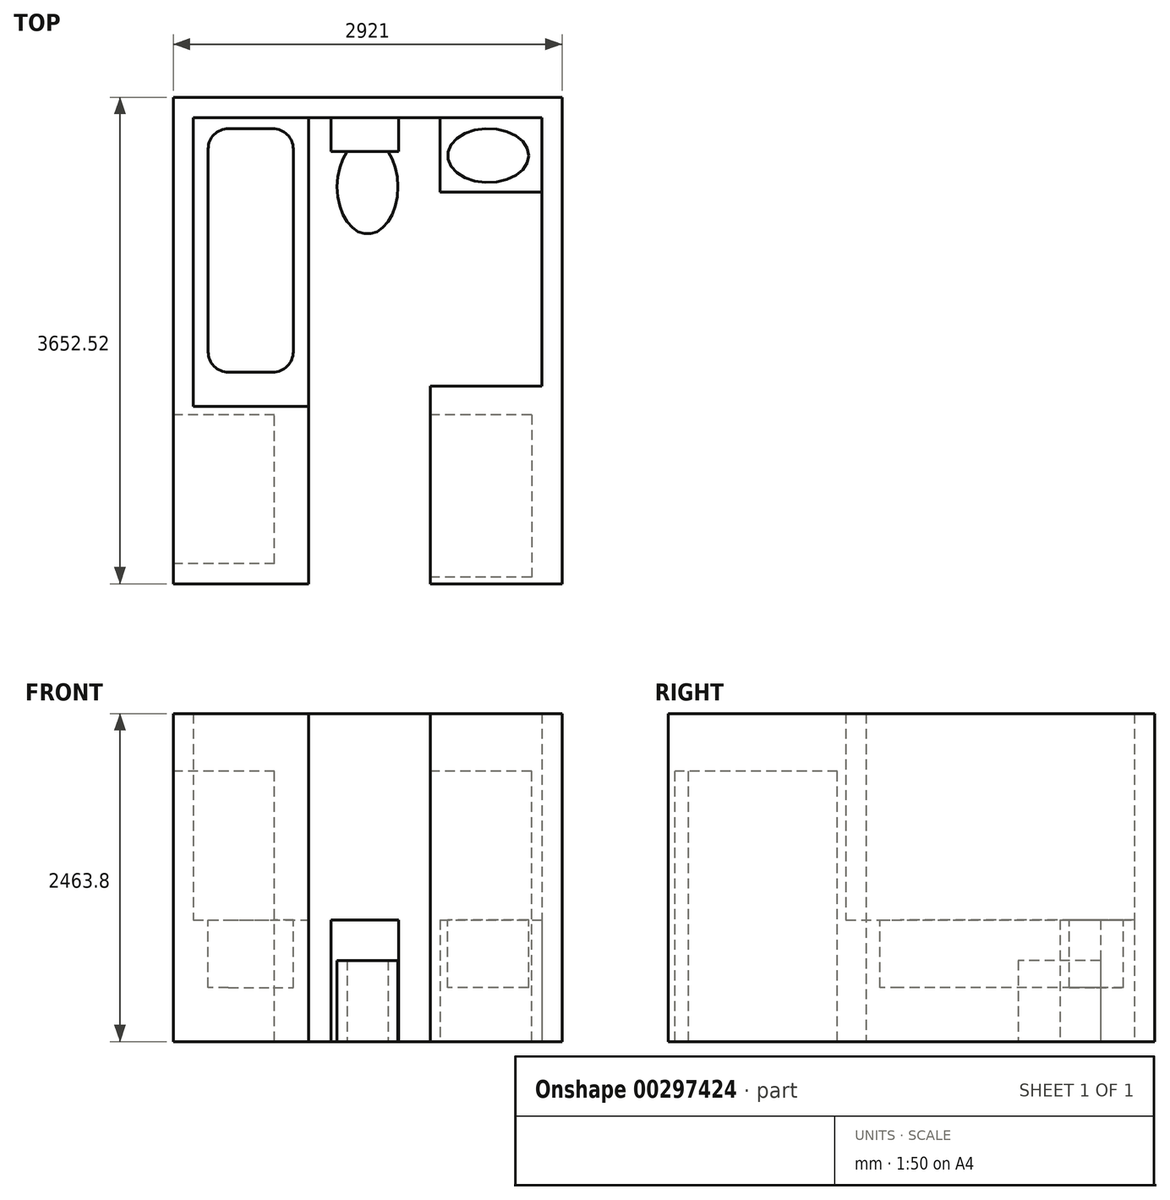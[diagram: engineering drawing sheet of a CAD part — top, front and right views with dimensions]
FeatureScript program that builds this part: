
annotation { "Feature Type Name" : "Feature", "Feature Type Description" : "" }
export const myFeature = defineFeature(function(context is Context, id is Id, definition is map)
    precondition{}
    {
        {
            var Q0;
            Q0=qCreatedBy(makeId("Top.planeOp"),FACE);
            var sketch = newSketch(context, id + "F0", { "sketchPlane" : qUnion([Q0])});
            skLineSegment(sketch, "E0.bottom", {"start": v(-1198.42, 0) * mm, "end": v(-334.82, 0) * mm});
            skLineSegment(sketch, "E0.top", {"start": v(-1350.82, -1333.5) * mm, "end": v(-334.82, -1333.5) * mm});
            skLineSegment(sketch, "E0.left", {"start": v(-1350.82, 0) * mm, "end": v(-1350.82, -1333.5) * mm});
            skLineSegment(sketch, "E0.right", {"start": v(-334.82, 0) * mm, "end": v(-334.82, -1333.5) * mm});
            skLineSegment(sketch, "E1.bottom", {"start": v(579.58, 0) * mm, "end": v(1417.78, 0) * mm});
            skLineSegment(sketch, "E1.top", {"start": v(579.58, -1333.5) * mm, "end": v(1570.18, -1333.5) * mm});
            skLineSegment(sketch, "E1.left", {"start": v(579.58, 0) * mm, "end": v(579.58, -1333.5) * mm});
            skLineSegment(sketch, "E1.right", {"start": v(1570.18, 0) * mm, "end": v(1570.18, -1333.5) * mm});
            skLineSegment(sketch, "E2", {"start": v(-1350.82, 0) * mm, "end": v(-1350.82, 2319.02) * mm});
            skLineSegment(sketch, "E3", {"start": v(-1350.82, 2319.02) * mm, "end": v(1570.18, 2319.02) * mm});
            skLineSegment(sketch, "E4", {"start": v(1570.18, 0) * mm, "end": v(1570.18, 2319.02) * mm});
            skLineSegment(sketch, "E5.0", {"start": v(-1198.42, 0) * mm, "end": v(-1198.42, 2166.62) * mm});
            skLineSegment(sketch, "E6.0", {"start": v(-1198.42, 2166.62) * mm, "end": v(1417.78, 2166.62) * mm});
            skLineSegment(sketch, "E7.0", {"start": v(1417.78, 0) * mm, "end": v(1417.78, 2166.62) * mm});
            skSolve(sketch);
        }
        {
            var Q0;
            Q0=qSketchRegion(id+"F0",true);
            extrude(context, id + "F1", {"entities" : qUnion([Q0]), "depth" : 2463.8 * mm});
        }
        {
            var Q0;
            Q0=makeQuery(id+"F1.opExtrude","SWEPT_FACE",FACE,{"disambiguationData":[OSD([sQuery(id+"F0.wireOp",EDGE,"E0.left"),sQuery(id+"F0.wireOp",EDGE,"E2")])]});
            var sketch = newSketch(context, id + "F2", { "sketchPlane" : qUnion([Q0])});
            skLineSegment(sketch, "E8.bottom", {"start": v(63.5, 0) * mm, "end": v(1181.1, 0) * mm});
            skLineSegment(sketch, "E8.top", {"start": v(63.5, 2032) * mm, "end": v(1181.1, 2032) * mm});
            skLineSegment(sketch, "E8.left", {"start": v(63.5, 0) * mm, "end": v(63.5, 2032) * mm});
            skLineSegment(sketch, "E8.right", {"start": v(1181.1, 0) * mm, "end": v(1181.1, 2032) * mm});
            skSolve(sketch);
        }
        {
            var Q0;
            Q0=makeQuery(id+"F2.imprint","IMPRINT",FACE,{"disambiguationData":[TD([[makeQuery(id+"F2.imprint","IMPRINT",EDGE,{"derivedFrom":sQuery(id+"F2.wireOp",EDGE,"E8.bottom")}),-1.0]])]});
            extrude(context, id + "F3", {"entities" : qUnion([Q0]), "operationType" : NewBodyOperationType.REMOVE, "oppositeDirection" : true, "depth" : 762 * mm});
        }
        {
            var Q0;
            Q0=makeQuery(id+"F1.opExtrude","SWEPT_FACE",FACE,{"disambiguationData":[OSD([sQuery(id+"F0.wireOp",EDGE,"E1.left")])]});
            var sketch = newSketch(context, id + "F4", { "sketchPlane" : qUnion([Q0])});
            skLineSegment(sketch, "E9.bottom", {"start": v(63.5, 0) * mm, "end": v(1282.7, 0) * mm});
            skLineSegment(sketch, "E9.top", {"start": v(63.5, 2032) * mm, "end": v(1282.7, 2032) * mm});
            skLineSegment(sketch, "E9.left", {"start": v(63.5, 0) * mm, "end": v(63.5, 2032) * mm});
            skLineSegment(sketch, "E9.right", {"start": v(1282.7, 0) * mm, "end": v(1282.7, 2032) * mm});
            skSolve(sketch);
        }
        {
            var Q0;
            Q0=makeQuery(id+"F4.imprint","IMPRINT",FACE,{"disambiguationData":[TD([[makeQuery(id+"F4.imprint","IMPRINT",EDGE,{"derivedFrom":sQuery(id+"F4.wireOp",EDGE,"E9.bottom")}),1.0]])]});
            extrude(context, id + "F5", {"entities" : qUnion([Q0]), "operationType" : NewBodyOperationType.REMOVE, "oppositeDirection" : true, "depth" : 762 * mm});
        }
        {
            var Q0;
            Q0=makeQuery(id+"F1.opExtrude","CAP_FACE",FACE,{"disambiguationData":[OSD([sQuery(id+"F0.wireOp",EDGE,"E0.bottom"),sQuery(id+"F0.wireOp",EDGE,"E0.top"),sQuery(id+"F0.wireOp",EDGE,"E0.left"),sQuery(id+"F0.wireOp",EDGE,"E0.right"),sQuery(id+"F0.wireOp",EDGE,"E1.bottom"),sQuery(id+"F0.wireOp",EDGE,"E1.top"),sQuery(id+"F0.wireOp",EDGE,"E1.left"),sQuery(id+"F0.wireOp",EDGE,"E1.right"),sQuery(id+"F0.wireOp",EDGE,"E2"),sQuery(id+"F0.wireOp",EDGE,"E3"),sQuery(id+"F0.wireOp",EDGE,"E4"),sQuery(id+"F0.wireOp",EDGE,"E5.0"),sQuery(id+"F0.wireOp",EDGE,"E6.0"),sQuery(id+"F0.wireOp",EDGE,"E7.0")])],"isStart":true});
            var sketch = newSketch(context, id + "F6", { "sketchPlane" : qUnion([Q0])});
            skLineSegment(sketch, "E10.bottom", {"start": v(1417.78, -2166.62) * mm, "end": v(655.78, -2166.62) * mm});
            skLineSegment(sketch, "E10.top", {"start": v(1417.78, -1607.82) * mm, "end": v(655.78, -1607.82) * mm});
            skLineSegment(sketch, "E10.left", {"start": v(1417.78, -2166.62) * mm, "end": v(1417.78, -1607.82) * mm});
            skLineSegment(sketch, "E10.right", {"start": v(655.78, -2166.62) * mm, "end": v(655.78, -1607.82) * mm});
            skLineSegment(sketch, "E11.bottom", {"start": v(-1198.42, -2166.62) * mm, "end": v(-334.82, -2166.62) * mm});
            skLineSegment(sketch, "E11.top", {"start": v(-1198.42, 0) * mm, "end": v(-334.82, 0) * mm});
            skLineSegment(sketch, "E11.left", {"start": v(-1198.42, -2166.62) * mm, "end": v(-1198.42, 0) * mm});
            skLineSegment(sketch, "E11.right", {"start": v(-334.82, -2166.62) * mm, "end": v(-334.82, 0) * mm});
            skLineSegment(sketch, "E12.bottom", {"start": v(-165.39, -2166.62) * mm, "end": v(342.61, -2166.62) * mm});
            skLineSegment(sketch, "E12.top", {"start": v(-165.39, -1912.62) * mm, "end": v(342.61, -1912.62) * mm});
            skLineSegment(sketch, "E12.left", {"start": v(-165.39, -2166.62) * mm, "end": v(-165.39, -1912.62) * mm});
            skLineSegment(sketch, "E12.right", {"start": v(342.61, -2166.62) * mm, "end": v(342.61, -1912.62) * mm});
            skSolve(sketch);
        }
        {
            var Q0;
            Q0=qSketchRegion(id+"F6",true);
            extrude(context, id + "F7", {"entities" : qUnion([Q0]), "operationType" : NewBodyOperationType.ADD, "oppositeDirection" : true, "depth" : 914.4 * mm});
        }
        {
            var Q0;
            Q0=makeQuery(id+"F7.boolean.opBoolean","MERGE",FACE,{"derivedFrom":[makeQuery(id+"F1.opExtrude","CAP_FACE",FACE,{"disambiguationData":[OSD([sQuery(id+"F0.wireOp",EDGE,"E0.bottom"),sQuery(id+"F0.wireOp",EDGE,"E0.top"),sQuery(id+"F0.wireOp",EDGE,"E0.left"),sQuery(id+"F0.wireOp",EDGE,"E0.right"),sQuery(id+"F0.wireOp",EDGE,"E1.bottom"),sQuery(id+"F0.wireOp",EDGE,"E1.top"),sQuery(id+"F0.wireOp",EDGE,"E1.left"),sQuery(id+"F0.wireOp",EDGE,"E1.right"),sQuery(id+"F0.wireOp",EDGE,"E2"),sQuery(id+"F0.wireOp",EDGE,"E3"),sQuery(id+"F0.wireOp",EDGE,"E4"),sQuery(id+"F0.wireOp",EDGE,"E5.0"),sQuery(id+"F0.wireOp",EDGE,"E6.0"),sQuery(id+"F0.wireOp",EDGE,"E7.0")])],"isStart":true}),makeQuery(id+"F7.opExtrude","CAP_FACE",FACE,{"disambiguationData":[OSD([sQuery(id+"F6.wireOp",EDGE,"E10.bottom"),sQuery(id+"F6.wireOp",EDGE,"E10.top"),sQuery(id+"F6.wireOp",EDGE,"E10.left"),sQuery(id+"F6.wireOp",EDGE,"E10.right")])],"isStart":true}),makeQuery(id+"F7.opExtrude","CAP_FACE",FACE,{"disambiguationData":[OSD([sQuery(id+"F6.wireOp",EDGE,"E11.bottom"),sQuery(id+"F6.wireOp",EDGE,"E11.top"),sQuery(id+"F6.wireOp",EDGE,"E11.left"),sQuery(id+"F6.wireOp",EDGE,"E11.right")])],"isStart":true}),makeQuery(id+"F7.opExtrude","CAP_FACE",FACE,{"disambiguationData":[OSD([sQuery(id+"F6.wireOp",EDGE,"E12.bottom"),sQuery(id+"F6.wireOp",EDGE,"E12.top"),sQuery(id+"F6.wireOp",EDGE,"E12.left"),sQuery(id+"F6.wireOp",EDGE,"E12.right")])],"isStart":true})]});
            var sketch = newSketch(context, id + "F8", { "sketchPlane" : qUnion([Q0])});
            skEllipse(sketch, "E13", {"center": v(109.68, -1649.28) * mm, "majorRadius": 355.6 * mm, "minorRadius": 228.6 * mm, "majorAxis": v(0, 1)});
            skSolve(sketch);
        }
        {
            var Q0;
            Q0=qSketchRegion(id+"F8",true);
            extrude(context, id + "F9", {"entities" : qUnion([Q0]), "operationType" : NewBodyOperationType.ADD, "oppositeDirection" : true, "depth" : 609.6 * mm});
        }
        {
            var Q0;
            Q0=makeQuery(id+"F7.opExtrude","CAP_FACE",FACE,{"disambiguationData":[OSD([sQuery(id+"F6.wireOp",EDGE,"E11.bottom"),sQuery(id+"F6.wireOp",EDGE,"E11.top"),sQuery(id+"F6.wireOp",EDGE,"E11.left"),sQuery(id+"F6.wireOp",EDGE,"E11.right")])],"isStart":false});
            var sketch = newSketch(context, id + "F10", { "sketchPlane" : qUnion([Q0])});
            skLineSegment(sketch, "E14.bottom", {"start": v(-935.5, 2085.16) * mm, "end": v(-601.52, 2085.16) * mm});
            skLineSegment(sketch, "E14.top", {"start": v(-935.5, 256.36) * mm, "end": v(-601.52, 256.36) * mm});
            skLineSegment(sketch, "E14.left", {"start": v(-1087.9, 1932.76) * mm, "end": v(-1087.9, 408.76) * mm});
            skLineSegment(sketch, "E15", {"start": v(-449.12, 1932.76) * mm, "end": v(-449.12, 408.76) * mm});
            skPoint(sketch, "E16.visualSharp", {"position": v(-1087.9, 2085.16) * mm});
            skArc(sketch, "E16.filletArc", {"start": v(-935.5, 2085.16) * mm, "mid": v(-1043.26, 2040.52) * mm, "end": v(-1087.9, 1932.76) * mm});
            skPoint(sketch, "E17.visualSharp", {"position": v(-449.12, 2085.16) * mm});
            skArc(sketch, "E17.filletArc", {"start": v(-449.12, 1932.76) * mm, "mid": v(-493.76, 2040.52) * mm, "end": v(-601.52, 2085.16) * mm});
            skPoint(sketch, "E18.visualSharp", {"position": v(-1087.9, 256.36) * mm});
            skArc(sketch, "E18.filletArc", {"start": v(-1087.9, 408.76) * mm, "mid": v(-1043.26, 301) * mm, "end": v(-935.5, 256.36) * mm});
            skPoint(sketch, "E19.visualSharp", {"position": v(-449.12, 256.36) * mm});
            skArc(sketch, "E19.filletArc", {"start": v(-601.52, 256.36) * mm, "mid": v(-493.76, 301) * mm, "end": v(-449.12, 408.76) * mm});
            skEllipse(sketch, "E20", {"center": v(1016.17, 1882.7) * mm, "majorRadius": 304.8 * mm, "minorRadius": 203.2 * mm, "majorAxis": v(1, 0)});
            skSolve(sketch);
        }
        {
            var Q0;
            Q0=qSketchRegion(id+"F10",true);
            extrude(context, id + "F11", {"entities" : qUnion([Q0]), "operationType" : NewBodyOperationType.REMOVE, "oppositeDirection" : true, "depth" : 508 * mm});
        }
        {
            var Q0;
            Q0=makeQuery(id+"F9.boolean.opBoolean","MERGE",FACE,{"derivedFrom":[makeQuery(id+"F7.boolean.opBoolean","MERGE",FACE,{"derivedFrom":[makeQuery(id+"F1.opExtrude","CAP_FACE",FACE,{"disambiguationData":[OSD([sQuery(id+"F0.wireOp",EDGE,"E0.bottom"),sQuery(id+"F0.wireOp",EDGE,"E0.top"),sQuery(id+"F0.wireOp",EDGE,"E0.left"),sQuery(id+"F0.wireOp",EDGE,"E0.right"),sQuery(id+"F0.wireOp",EDGE,"E1.bottom"),sQuery(id+"F0.wireOp",EDGE,"E1.top"),sQuery(id+"F0.wireOp",EDGE,"E1.left"),sQuery(id+"F0.wireOp",EDGE,"E1.right"),sQuery(id+"F0.wireOp",EDGE,"E2"),sQuery(id+"F0.wireOp",EDGE,"E3"),sQuery(id+"F0.wireOp",EDGE,"E4"),sQuery(id+"F0.wireOp",EDGE,"E5.0"),sQuery(id+"F0.wireOp",EDGE,"E6.0"),sQuery(id+"F0.wireOp",EDGE,"E7.0")])],"isStart":true}),makeQuery(id+"F7.opExtrude","CAP_FACE",FACE,{"disambiguationData":[OSD([sQuery(id+"F6.wireOp",EDGE,"E10.bottom"),sQuery(id+"F6.wireOp",EDGE,"E10.top"),sQuery(id+"F6.wireOp",EDGE,"E10.left"),sQuery(id+"F6.wireOp",EDGE,"E10.right")])],"isStart":true}),makeQuery(id+"F7.opExtrude","CAP_FACE",FACE,{"disambiguationData":[OSD([sQuery(id+"F6.wireOp",EDGE,"E11.bottom"),sQuery(id+"F6.wireOp",EDGE,"E11.top"),sQuery(id+"F6.wireOp",EDGE,"E11.left"),sQuery(id+"F6.wireOp",EDGE,"E11.right")])],"isStart":true}),makeQuery(id+"F7.opExtrude","CAP_FACE",FACE,{"disambiguationData":[OSD([sQuery(id+"F6.wireOp",EDGE,"E12.bottom"),sQuery(id+"F6.wireOp",EDGE,"E12.top"),sQuery(id+"F6.wireOp",EDGE,"E12.left"),sQuery(id+"F6.wireOp",EDGE,"E12.right")])],"isStart":true})]}),makeQuery(id+"F9.opExtrude","CAP_FACE",FACE,{"disambiguationData":[OSD([sQuery(id+"F8.wireOp",EDGE,"E13")])],"isStart":true})]});
            var sketch = newSketch(context, id + "F12", { "sketchPlane" : qUnion([Q0])});
            skLineSegment(sketch, "E21.bottom", {"start": v(579.58, 0) * mm, "end": v(1417.78, 0) * mm});
            skLineSegment(sketch, "E21.top", {"start": v(579.58, -152.4) * mm, "end": v(1417.78, -152.4) * mm});
            skLineSegment(sketch, "E21.left", {"start": v(579.58, 0) * mm, "end": v(579.58, -152.4) * mm});
            skLineSegment(sketch, "E21.right", {"start": v(1417.78, 0) * mm, "end": v(1417.78, -152.4) * mm});
            skLineSegment(sketch, "E22.bottom", {"start": v(-1198.42, 0) * mm, "end": v(-1350.82, 0) * mm});
            skLineSegment(sketch, "E22.top", {"start": v(-1198.42, -152.4) * mm, "end": v(-1350.82, -152.4) * mm});
            skLineSegment(sketch, "E22.left", {"start": v(-1350.82, 0) * mm, "end": v(-1350.82, -152.4) * mm});
            skLineSegment(sketch, "E22.right", {"start": v(-1198.42, 0) * mm, "end": v(-1198.42, -152.4) * mm});
            skSolve(sketch);
        }
        {
            var Q0;
            Q0=qSketchRegion(id+"F12",true);
            var Q1;
            Q1=makeQuery(id+"F1.opExtrude","CAP_FACE",FACE,{"disambiguationData":[OSD([sQuery(id+"F0.wireOp",EDGE,"E0.bottom"),sQuery(id+"F0.wireOp",EDGE,"E0.top"),sQuery(id+"F0.wireOp",EDGE,"E0.left"),sQuery(id+"F0.wireOp",EDGE,"E0.right"),sQuery(id+"F0.wireOp",EDGE,"E1.bottom"),sQuery(id+"F0.wireOp",EDGE,"E1.top"),sQuery(id+"F0.wireOp",EDGE,"E1.left"),sQuery(id+"F0.wireOp",EDGE,"E1.right"),sQuery(id+"F0.wireOp",EDGE,"E2"),sQuery(id+"F0.wireOp",EDGE,"E3"),sQuery(id+"F0.wireOp",EDGE,"E4"),sQuery(id+"F0.wireOp",EDGE,"E5.0"),sQuery(id+"F0.wireOp",EDGE,"E6.0"),sQuery(id+"F0.wireOp",EDGE,"E7.0")])],"isStart":false});
            extrude(context, id + "F13", {"entities" : qUnion([Q0]), "operationType" : NewBodyOperationType.ADD, "endBound" : BoundingType.UP_TO_SURFACE, "oppositeDirection" : true, "endBoundEntityFace" : qUnion([Q1]), "depth" : 25.4 * mm});
        }
    });
